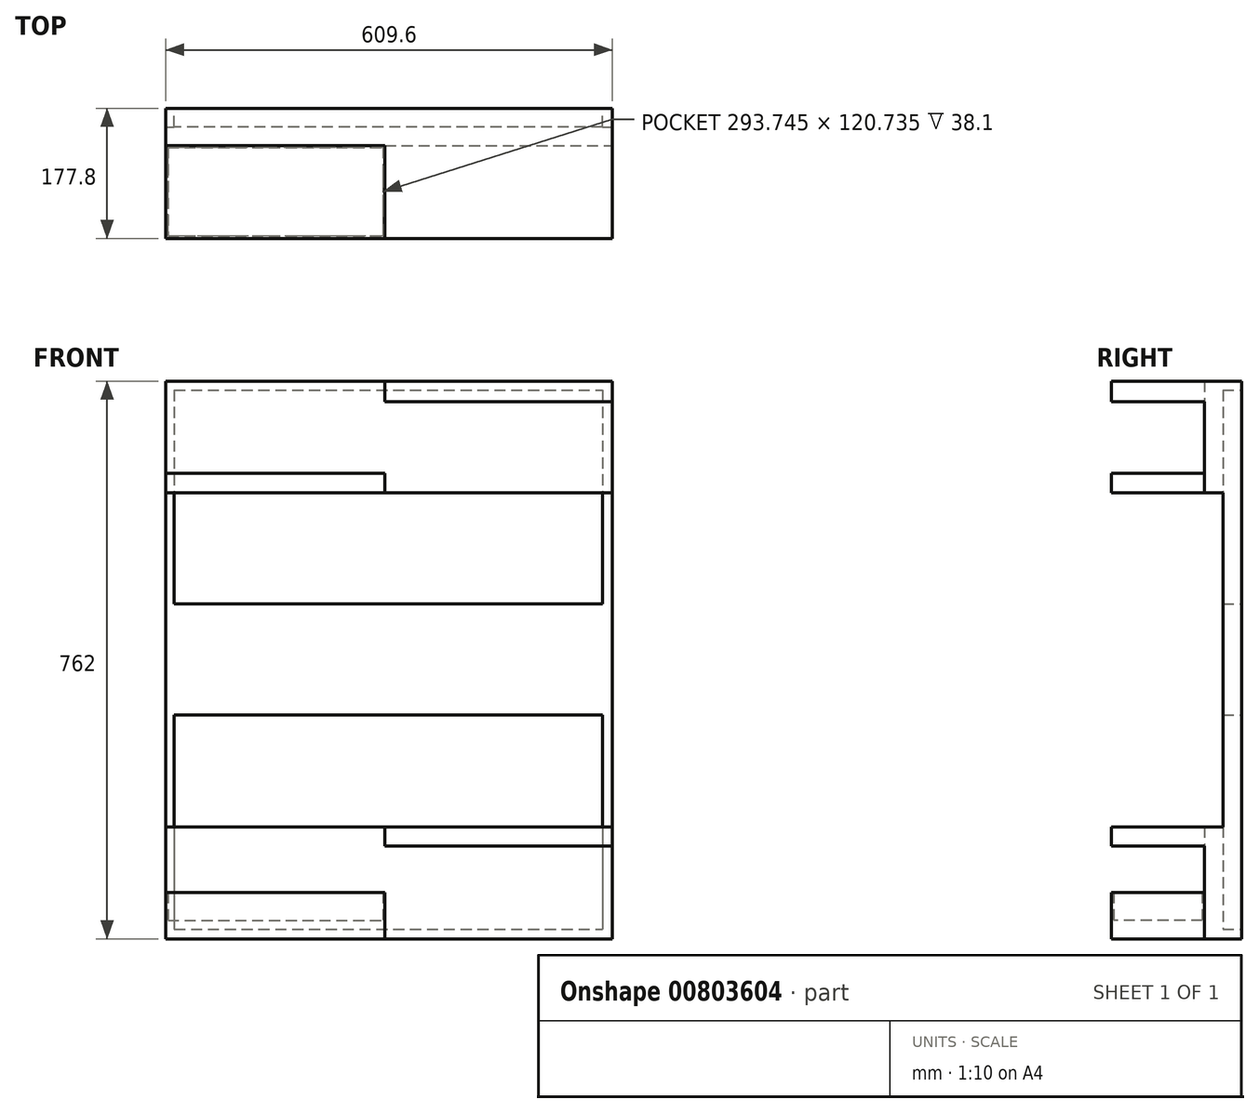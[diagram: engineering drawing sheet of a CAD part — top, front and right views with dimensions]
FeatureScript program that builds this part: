
annotation { "Feature Type Name" : "Feature", "Feature Type Description" : "" }
export const myFeature = defineFeature(function(context is Context, id is Id, definition is map)
    precondition{}
    {
        {
            var Q0;
            Q0=qCreatedBy(makeId("Front.planeOp"),FACE);
            var sketch = newSketch(context, id + "F0", { "sketchPlane" : qUnion([Q0])});
            skLineSegment(sketch, "E0.bottom", {"start": v(-299.24, 455.87) * mm, "end": v(310.36, 455.87) * mm});
            skLineSegment(sketch, "E0.top", {"start": v(-299.24, -306.13) * mm, "end": v(310.36, -306.13) * mm});
            skLineSegment(sketch, "E0.left", {"start": v(-299.24, 455.87) * mm, "end": v(-299.24, -306.13) * mm});
            skLineSegment(sketch, "E0.right", {"start": v(310.36, 455.87) * mm, "end": v(310.36, -306.13) * mm});
            skLineSegment(sketch, "E1.bottom", {"start": v(-287.5, 443.52) * mm, "end": v(297.02, 443.52) * mm});
            skLineSegment(sketch, "E1.top", {"start": v(-287.5, -293.3) * mm, "end": v(297.02, -293.3) * mm});
            skLineSegment(sketch, "E1.left", {"start": v(-287.5, 443.52) * mm, "end": v(-287.5, -293.3) * mm});
            skLineSegment(sketch, "E1.right", {"start": v(297.02, 443.52) * mm, "end": v(297.02, -293.3) * mm});
            skSolve(sketch);
        }
        {
            var Q0;
            Q0=makeQuery(id+"F0.imprint","IMPRINT",FACE,{"disambiguationData":[TD([[makeQuery(id+"F0.imprint","IMPRINT",EDGE,{"derivedFrom":sQuery(id+"F0.wireOp",EDGE,"E0.bottom")}),-1.0]])]});
            extrude(context, id + "F1", {"entities" : qUnion([Q0]), "depth" : 25.4 * mm, "offsetDistance" : 25.4 * mm});
        }
        {
            var Q0;
            Q0=makeQuery(id+"F1.opExtrude","CAP_FACE",FACE,{"disambiguationData":[OSD([sQuery(id+"F0.wireOp",EDGE,"E0.bottom"),sQuery(id+"F0.wireOp",EDGE,"E0.top"),sQuery(id+"F0.wireOp",EDGE,"E0.left"),sQuery(id+"F0.wireOp",EDGE,"E0.right"),sQuery(id+"F0.wireOp",EDGE,"E1.bottom"),sQuery(id+"F0.wireOp",EDGE,"E1.top"),sQuery(id+"F0.wireOp",EDGE,"E1.left"),sQuery(id+"F0.wireOp",EDGE,"E1.right")])],"isStart":false});
            var sketch = newSketch(context, id + "F2", { "sketchPlane" : qUnion([Q0])});
            skLineSegment(sketch, "E2.bottom", {"start": v(-299.24, 455.87) * mm, "end": v(310.36, 455.87) * mm});
            skLineSegment(sketch, "E2.top", {"start": v(-299.24, 303.47) * mm, "end": v(310.36, 303.47) * mm});
            skLineSegment(sketch, "E2.left", {"start": v(-299.24, 455.87) * mm, "end": v(-299.24, 303.47) * mm});
            skLineSegment(sketch, "E2.right", {"start": v(310.36, 455.87) * mm, "end": v(310.36, 303.47) * mm});
            skSolve(sketch);
        }
        {
            var Q0;
            {var subQ5=makeQuery(id+"F1.opExtrude","CAP_EDGE",EDGE,{"disambiguationData":[OSD([sQuery(id+"F0.wireOp",EDGE,"E1.bottom")])],"isStart":false});Q0=makeQuery(id+"F2.imprint","IMPRINT",FACE,{"disambiguationData":[TD([[makeQuery(id+"F2.imprint","IMPRINT",EDGE,{"derivedFrom":subQ5}),-1.0]])]});}
            var Q1;
            Q1=makeQuery(id+"F2.imprint","IMPRINT",FACE,{"disambiguationData":[TD([[makeQuery(id+"F2.imprint","IMPRINT",EDGE,{"derivedFrom":sQuery(id+"F2.wireOp",EDGE,"E2.bottom")}),-1.0]])]});
            extrude(context, id + "F3", {"entities" : qUnion([Q0, Q1]), "operationType" : NewBodyOperationType.ADD, "depth" : 25.4 * mm, "offsetDistance" : 25.4 * mm});
        }
        {
            var Q0;
            Q0=makeQuery(id+"F1.opExtrude","CAP_FACE",FACE,{"disambiguationData":[OSD([sQuery(id+"F0.wireOp",EDGE,"E0.bottom"),sQuery(id+"F0.wireOp",EDGE,"E0.top"),sQuery(id+"F0.wireOp",EDGE,"E0.left"),sQuery(id+"F0.wireOp",EDGE,"E0.right"),sQuery(id+"F0.wireOp",EDGE,"E1.bottom"),sQuery(id+"F0.wireOp",EDGE,"E1.top"),sQuery(id+"F0.wireOp",EDGE,"E1.left"),sQuery(id+"F0.wireOp",EDGE,"E1.right")])],"isStart":false});
            var sketch = newSketch(context, id + "F4", { "sketchPlane" : qUnion([Q0])});
            skLineSegment(sketch, "E3.bottom", {"start": v(-299.24, -306.13) * mm, "end": v(310.36, -306.13) * mm});
            skLineSegment(sketch, "E3.top", {"start": v(-299.24, -153.15) * mm, "end": v(310.36, -153.15) * mm});
            skLineSegment(sketch, "E3.left", {"start": v(-299.24, -306.13) * mm, "end": v(-299.24, -153.15) * mm});
            skLineSegment(sketch, "E3.right", {"start": v(310.36, -306.13) * mm, "end": v(310.36, -153.15) * mm});
            skSolve(sketch);
        }
        {
            var Q0;
            Q0 = qSketchRegion(id + "F4", true);
            extrude(context, id + "F5", {"entities" : qUnion([Q0]), "operationType" : NewBodyOperationType.ADD, "depth" : 25.4 * mm, "offsetDistance" : 25.4 * mm});
        }
        {
            var Q0;
            Q0=qCreatedBy(makeId("Front.planeOp"),FACE);
            var sketch = newSketch(context, id + "F6", { "sketchPlane" : qUnion([Q0])});
            skLineSegment(sketch, "E4.bottom", {"start": v(309.4, 151.18) * mm, "end": v(-298.27, 151.18) * mm});
            skLineSegment(sketch, "E4.top", {"start": v(309.4, 0) * mm, "end": v(-298.27, 0) * mm});
            skLineSegment(sketch, "E4.left", {"start": v(309.4, 151.18) * mm, "end": v(309.4, 0) * mm});
            skLineSegment(sketch, "E4.right", {"start": v(-298.27, 151.18) * mm, "end": v(-298.27, 0) * mm});
            skSolve(sketch);
        }
        {
            var Q0;
            Q0 = qSketchRegion(id + "F6", true);
            extrude(context, id + "F7", {"entities" : qUnion([Q0]), "operationType" : NewBodyOperationType.ADD, "depth" : 25.4 * mm, "offsetDistance" : 25.4 * mm});
        }
        {
            var Q0;
            Q0=makeQuery(id+"F5.opExtrude","CAP_FACE",FACE,{"disambiguationData":[OSD([sQuery(id+"F4.wireOp",EDGE,"E3.bottom"),sQuery(id+"F4.wireOp",EDGE,"E3.top"),sQuery(id+"F4.wireOp",EDGE,"E3.left"),sQuery(id+"F4.wireOp",EDGE,"E3.right")])],"isStart":false});
            var sketch = newSketch(context, id + "F8", { "sketchPlane" : qUnion([Q0])});
            skLineSegment(sketch, "E5.bottom", {"start": v(310.36, -153.15) * mm, "end": v(0, -153.15) * mm});
            skLineSegment(sketch, "E5.top", {"start": v(310.36, -179.5) * mm, "end": v(0, -179.5) * mm});
            skLineSegment(sketch, "E5.left", {"start": v(310.36, -153.15) * mm, "end": v(310.36, -179.5) * mm});
            skLineSegment(sketch, "E5.right", {"start": v(0, -153.15) * mm, "end": v(0, -179.5) * mm});
            skSolve(sketch);
        }
        {
            var Q0;
            Q0=makeQuery(id+"F8.imprint","IMPRINT",FACE,{"disambiguationData":[TD([[makeQuery(id+"F8.imprint","IMPRINT",EDGE,{"derivedFrom":sQuery(id+"F8.wireOp",EDGE,"E5.bottom")}),-1.0]])]});
            extrude(context, id + "F9", {"entities" : qUnion([Q0]), "operationType" : NewBodyOperationType.ADD, "depth" : 127 * mm, "offsetDistance" : 25.4 * mm});
        }
        {
            var Q0;
            Q0=makeQuery(id+"F5.opExtrude","CAP_FACE",FACE,{"disambiguationData":[OSD([sQuery(id+"F4.wireOp",EDGE,"E3.bottom"),sQuery(id+"F4.wireOp",EDGE,"E3.top"),sQuery(id+"F4.wireOp",EDGE,"E3.left"),sQuery(id+"F4.wireOp",EDGE,"E3.right")])],"isStart":false});
            var sketch = newSketch(context, id + "F10", { "sketchPlane" : qUnion([Q0])});
            skLineSegment(sketch, "E6.bottom", {"start": v(-299.24, -306.13) * mm, "end": v(0, -306.13) * mm});
            skLineSegment(sketch, "E6.top", {"start": v(-299.24, -280.73) * mm, "end": v(0, -280.73) * mm});
            skLineSegment(sketch, "E6.left", {"start": v(-299.24, -306.13) * mm, "end": v(-299.24, -280.73) * mm});
            skLineSegment(sketch, "E6.right", {"start": v(0, -306.13) * mm, "end": v(0, -280.73) * mm});
            skSolve(sketch);
        }
        {
            var Q0;
            Q0 = qSketchRegion(id + "F10", true);
            extrude(context, id + "F11", {"entities" : qUnion([Q0]), "operationType" : NewBodyOperationType.ADD, "depth" : 127 * mm, "offsetDistance" : 25.4 * mm});
        }
        {
            var Q0;
            Q0=makeQuery(id+"F11.opExtrude","SWEPT_FACE",FACE,{"disambiguationData":[OSD([sQuery(id+"F10.wireOp",EDGE,"E6.top")])]});
            var sketch = newSketch(context, id + "F12", { "sketchPlane" : qUnion([Q0])});
            skLineSegment(sketch, "E7.bottom", {"start": v(-296.22, -53.56) * mm, "end": v(-2.48, -53.56) * mm});
            skLineSegment(sketch, "E7.top", {"start": v(-296.22, -174.3) * mm, "end": v(-2.48, -174.3) * mm});
            skLineSegment(sketch, "E7.left", {"start": v(-296.22, -53.56) * mm, "end": v(-296.22, -174.3) * mm});
            skLineSegment(sketch, "E7.right", {"start": v(-2.48, -53.56) * mm, "end": v(-2.48, -174.3) * mm});
            skSolve(sketch);
        }
        {
            var Q0;
            Q0=makeQuery(id+"F12.imprint","IMPRINT",FACE,{"disambiguationData":[TD([[makeQuery(id+"F12.imprint","IMPRINT",EDGE,{"derivedFrom":sQuery(id+"F12.wireOp",EDGE,"E7.bottom")}),1.0]])]});
            extrude(context, id + "F13", {"entities" : qUnion([Q0]), "operationType" : NewBodyOperationType.ADD, "depth" : 38.1 * mm, "offsetDistance" : 25.4 * mm});
        }
        {
            var Q0;
            Q0=makeQuery(id+"F3.opExtrude","CAP_FACE",FACE,{"disambiguationData":[OSD([sQuery(id+"F2.wireOp",EDGE,"E2.bottom"),sQuery(id+"F2.wireOp",EDGE,"E2.top"),sQuery(id+"F2.wireOp",EDGE,"E2.left"),sQuery(id+"F2.wireOp",EDGE,"E2.right")])],"isStart":false});
            var sketch = newSketch(context, id + "F14", { "sketchPlane" : qUnion([Q0])});
            skLineSegment(sketch, "E8.bottom", {"start": v(-299.24, 303.47) * mm, "end": v(0, 303.47) * mm});
            skLineSegment(sketch, "E8.top", {"start": v(-299.24, 329.83) * mm, "end": v(0, 329.83) * mm});
            skLineSegment(sketch, "E8.left", {"start": v(-299.24, 303.47) * mm, "end": v(-299.24, 329.83) * mm});
            skLineSegment(sketch, "E8.right", {"start": v(0, 303.47) * mm, "end": v(0, 329.83) * mm});
            skLineSegment(sketch, "E9.bottom", {"start": v(0, 455.87) * mm, "end": v(310.36, 455.87) * mm});
            skLineSegment(sketch, "E9.top", {"start": v(0, 427.43) * mm, "end": v(310.36, 427.43) * mm});
            skLineSegment(sketch, "E9.left", {"start": v(0, 455.87) * mm, "end": v(0, 427.43) * mm});
            skLineSegment(sketch, "E9.right", {"start": v(310.36, 455.87) * mm, "end": v(310.36, 427.43) * mm});
            skLineSegment(sketch, "E10.bottom", {"start": v(0, 0) * mm, "end": v(-46.33, 0) * mm});
            skLineSegment(sketch, "E10.top", {"start": v(0, 27.5) * mm, "end": v(-46.33, 27.5) * mm});
            skLineSegment(sketch, "E10.left", {"start": v(0, 0) * mm, "end": v(0, 27.5) * mm});
            skLineSegment(sketch, "E10.right", {"start": v(-46.33, 0) * mm, "end": v(-46.33, 27.5) * mm});
            skSolve(sketch);
        }
        {
            var Q0;
            Q0=makeQuery(id+"F14.imprint","IMPRINT",FACE,{"disambiguationData":[TD([[makeQuery(id+"F14.imprint","IMPRINT",EDGE,{"derivedFrom":sQuery(id+"F14.wireOp",EDGE,"E8.bottom")}),1.0]])]});
            var Q1;
            Q1=makeQuery(id+"F14.imprint","IMPRINT",FACE,{"disambiguationData":[TD([[makeQuery(id+"F14.imprint","IMPRINT",EDGE,{"derivedFrom":sQuery(id+"F14.wireOp",EDGE,"E9.bottom")}),-1.0]])]});
            extrude(context, id + "F15", {"entities" : qUnion([Q0, Q1]), "operationType" : NewBodyOperationType.ADD, "depth" : 127 * mm, "offsetDistance" : 25.4 * mm});
        }
    });
